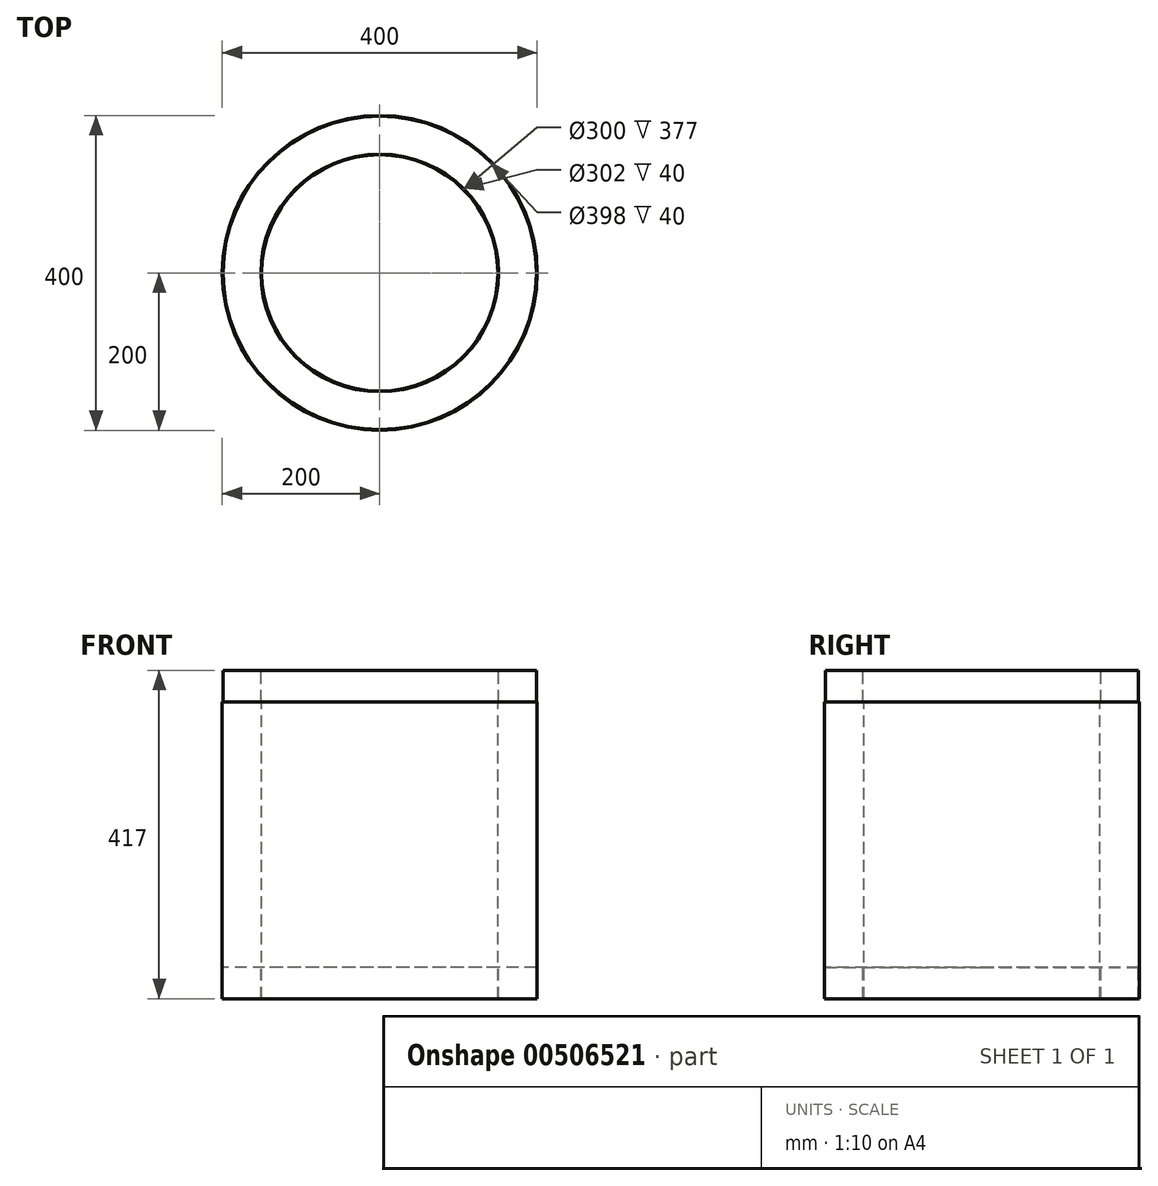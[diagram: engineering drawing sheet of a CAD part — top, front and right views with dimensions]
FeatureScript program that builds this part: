
annotation { "Feature Type Name" : "Feature", "Feature Type Description" : "" }
export const myFeature = defineFeature(function(context is Context, id is Id, definition is map)
    precondition{}
    {
        {
            var Q0;
            Q0=qCreatedBy(makeId("Front.planeOp"),FACE);
            var sketch = newSketch(context, id + "F0", { "sketchPlane" : qUnion([Q0])});
            skLineSegment(sketch, "E0", {"start": v(0, 74.87) * mm, "end": v(0, -73.71) * mm, "construction": true});
            skLineSegment(sketch, "E1", {"start": v(0, 374.84) * mm, "end": v(0, -528.94) * mm, "construction": true});
            skLineSegment(sketch, "E2", {"start": v(-150, -489.75) * mm, "end": v(-150, -112.75) * mm});
            skLineSegment(sketch, "E3", {"start": v(-150, -112.75) * mm, "end": v(-151, -112.75) * mm});
            skLineSegment(sketch, "E4", {"start": v(-151, -112.75) * mm, "end": v(-151, -72.75) * mm});
            skLineSegment(sketch, "E5", {"start": v(-151, -72.75) * mm, "end": v(-199, -72.75) * mm});
            skLineSegment(sketch, "E6", {"start": v(-199, -72.75) * mm, "end": v(-199, -112.75) * mm});
            skLineSegment(sketch, "E7", {"start": v(-199, -112.75) * mm, "end": v(-200, -112.75) * mm});
            skLineSegment(sketch, "E8", {"start": v(-200, -112.75) * mm, "end": v(-200, -489.75) * mm});
            skLineSegment(sketch, "E9", {"start": v(-200, -489.75) * mm, "end": v(-199, -489.75) * mm});
            skLineSegment(sketch, "E10", {"start": v(-199, -489.75) * mm, "end": v(-199, -449.75) * mm});
            skLineSegment(sketch, "E11", {"start": v(-199, -449.75) * mm, "end": v(-151, -449.75) * mm});
            skLineSegment(sketch, "E12", {"start": v(-151, -449.75) * mm, "end": v(-151, -489.75) * mm});
            skLineSegment(sketch, "E13", {"start": v(-151, -489.75) * mm, "end": v(-150, -489.75) * mm});
            skSolve(sketch);
        }
        {
            var Q0;
            Q0=qSketchRegion(id+"F0",true);
            var Q1;
            Q1=sQuery(id+"F0.wireOp",EDGE,"E1");
            revolve(context, id + "F1", {"entities" : qUnion([Q0]), "axis" : qUnion([Q1]), "revolveType" : RevolveType.FULL});
        }
    });
